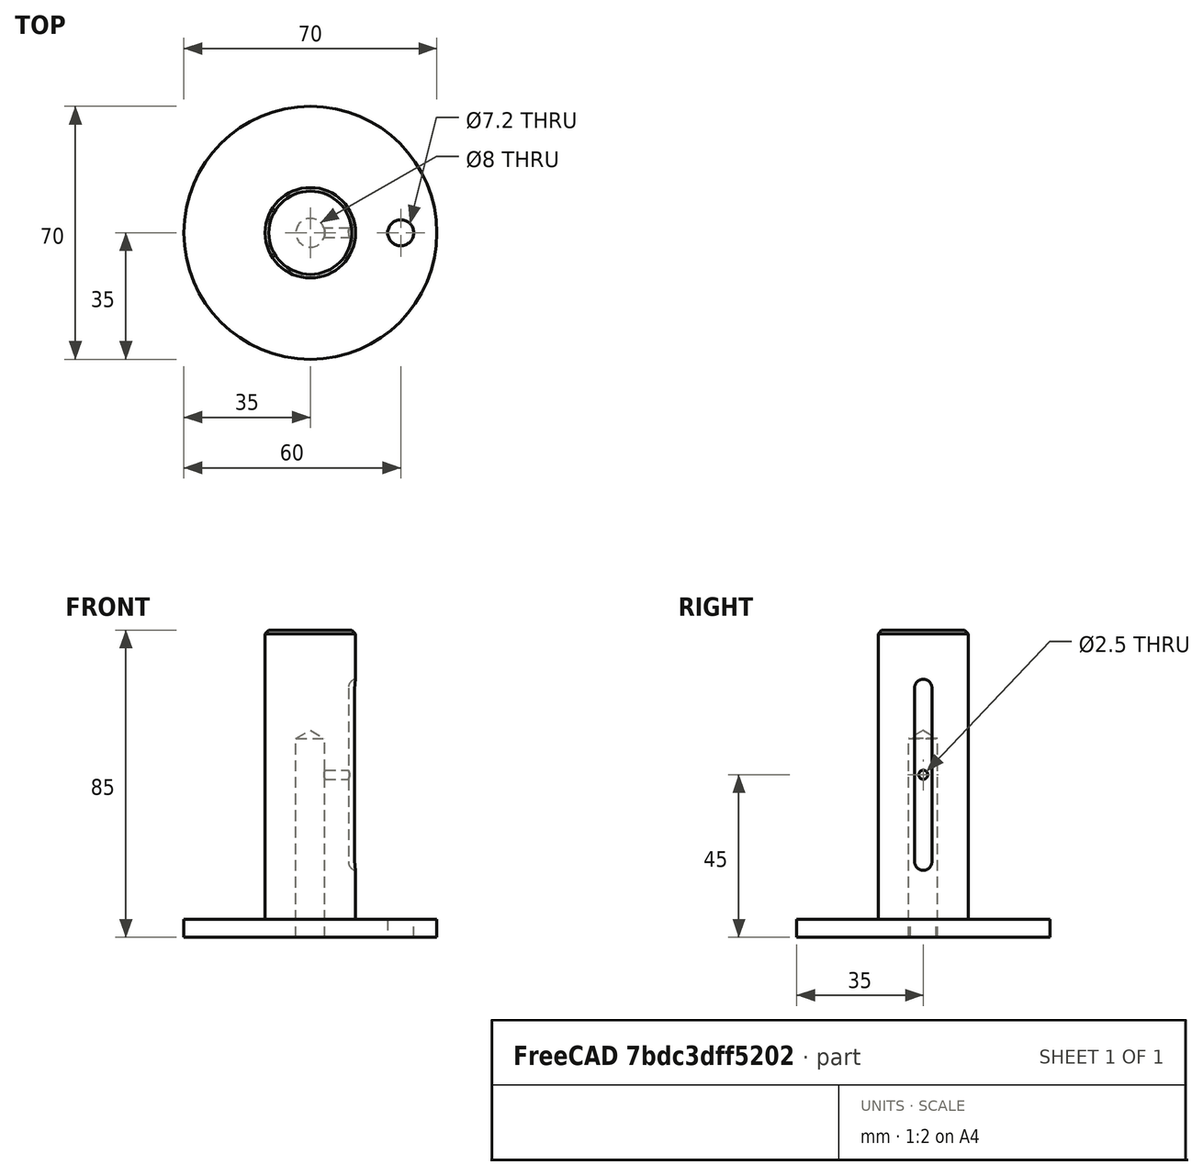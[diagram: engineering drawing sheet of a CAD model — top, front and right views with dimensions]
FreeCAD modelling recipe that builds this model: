
FCSTD DOCUMENT  (FreeCAD 0.20R29177 +426 (Git))
Label: hovair
License: All rights reserved
LicenseURL: http://en.wikipedia.org/wiki/All_rights_reserved
objects: Sketcher::SketchObject×8, TechDraw::DrawLeaderLine×5, TechDraw::DrawViewAnnotation×5, PartDesign::Plane×4, PartDesign::Pocket×4, TechDraw::DrawViewDimension×4, TechDraw::DrawViewSection×3, TechDraw::DrawViewBalloon×3, PartDesign::Revolution×2, PartDesign::Groove×2, PartDesign::Chamfer×2, TechDraw::DrawProjGroupItem×2, PartDesign::Body×1, TechDraw::DrawSVGTemplate×1, TechDraw::DrawProjGroup×1, TechDraw::DrawPage×1
note: 33 computed .brp shape members not serialized (recipe doc carries the construction recipe); baked Part::Feature solids carry a one-line shape summary decoded from their .brp

FEATURE [Sketcher::SketchObject] Sketch  label="axe sketch"
  FullyConstrained = true
  MapMode = 5
  Placement = pos=(0,0,0) rot=(1,0,0;1.5708rad)
  Support = -> [XZ_Plane]
  sketch-geometry (8):
    g0: LineSegment StartX=0 StartY=85 StartZ=0 EndX=-12.5 EndY=85 EndZ=0
    g1: LineSegment StartX=-12.5 StartY=85 StartZ=0 EndX=-12.5 EndY=5 EndZ=0
    g2: LineSegment StartX=-12.5 StartY=5 StartZ=0 EndX=-35 EndY=5 EndZ=0
    g3: LineSegment StartX=-35 StartY=5 StartZ=0 EndX=-35 EndY=0 EndZ=0
    g4: LineSegment StartX=-35 StartY=0 StartZ=0 EndX=-4 EndY=0 EndZ=0
    g5: LineSegment StartX=-4 StartY=0 StartZ=0 EndX=-4 EndY=55 EndZ=0
    g6: LineSegment StartX=-4 StartY=55 StartZ=0 EndX=0 EndY=57.3094 EndZ=0
    g7: LineSegment StartX=0 StartY=57.3094 StartZ=0 EndX=0 EndY=85 EndZ=0
  constraints (24):
    c: Horizontal(g0)
    c: Vertical(g1)
    c: Horizontal(g2)
    c: Vertical(g3)
    c: Horizontal(g4)
    c: Vertical(g5)
    c: Coincident(g6,g5)
    c: PointOnObject(g6,g-2)
    c: Coincident(g7,g6)
    c: Coincident(g0,g7)
    c: PointOnObject(g0,g-2)
    c: Coincident(g1,g0)
    c: Coincident(g2,g1)
    c: Coincident(g2,g3)
    c: Coincident(g4,g3)
    c: Coincident(g5,g4)
    c: Angle(g6,g-2) = 1.0472
    c: DistanceX(g4) = -4
    c: DistanceX(g3) = -35
    c: Distance(g3) = 5
    c: PointOnObject(g4,g-1)
    c: DistanceY(g1,g1) = 80
    c: Distance(g0) = 12.5
    c: DistanceY(g5) = 55
FEATURE [PartDesign::Revolution] Revolution  label="axe révolution"
  Angle = 360
  Axis = (0,2e-16,1)
  Base = (0,0,0)
  Placement = pos=(0,0,0) rot=(1,0,0;1.5708rad)
  Profile = -> Sketch
  ReferenceAxis = -> Sketch [V_Axis]
FEATURE [PartDesign::Plane] DatumPlane
  Length = 87.4941
  MapMode = 2
  Placement = pos=(0,0,0) rot=(1,0,0;1.5708rad)
  ResizeMode = 0
  Support = -> [Sketch]
  Width = 127.544
FEATURE [Sketcher::SketchObject] Sketch001  label="rainure sketch"
  FullyConstrained = false
  MapMode = 5
  Placement = pos=(0,0,0) rot=(1,0,0;1.5708rad)
  Support = -> [DatumPlane]
  sketch-geometry (5):
    g0: LineSegment StartX=13 StartY=71.5 StartZ=0 EndX=13 EndY=18.5 EndZ=0
    g1: LineSegment StartX=10.5 StartY=69 StartZ=0 EndX=10.5 EndY=21 EndZ=0
    g2: ArcOfCircle CenterX=13 CenterY=69 CenterZ=0 NormalX=0 NormalY=0 NormalZ=1 AngleXU=0 Radius=2.5 StartAngle=1.5708 EndAngle=3.14159
    g3: ArcOfCircle CenterX=13 CenterY=21 CenterZ=0 NormalX=0 NormalY=0 NormalZ=1 AngleXU=0 Radius=2.5 StartAngle=3.14159 EndAngle=4.71239
    g4: LineSegment StartX=13 StartY=82.5445 StartZ=0 EndX=13 EndY=14.5184 EndZ=0
  constraints (16):
    c: Vertical(g0)
    c: Vertical(g1)
    c: DistanceY(g0) = 18.5
    c: DistanceY(g1) = 21
    c: Distance(g1) = 48
    c: Distance(g0) = 53
    c: PointOnObject(g2,g0)
    c: Coincident(g2,g1)
    c: Coincident(g2,g0)
    c: Diameter(g2) = 5
    c: PointOnObject(g3,g0)
    c: Coincident(g3,g0)
    c: Coincident(g3,g1)
    c: DistanceX(g3) = 13
    c: Vertical(g4)
    c: PointOnObject(g2,g4)
FEATURE [PartDesign::Groove] Groove  label="rainure révolution"
  Angle = 360
  Axis = (0,-1.51e-14,-68.0261)
  Base = (13,1.83e-14,82.5445)
  BaseFeature = -> Revolution
  Placement = pos=(0,0,0) rot=(1,0,0;1.5708rad)
  Profile = -> Sketch001
  ReferenceAxis = -> Sketch001 [Axis0]
FEATURE [PartDesign::Plane] DatumPlane001
  AttachmentOffset = pos=(13,0,0) rot=(0,1,0;1.5708rad)
  Length = 87.522
  MapMode = 2
  Placement = pos=(13,0,0) rot=(0.57735,0.57735,0.57735;2.0944rad)
  ResizeMode = 0
  Support = -> [Sketch001]
  Width = 127.547
FEATURE [Sketcher::SketchObject] Sketch002  label="canal sketch"
  FullyConstrained = true
  MapMode = 5
  Placement = pos=(13,0,0) rot=(0.57735,0.57735,0.57735;2.0944rad)
  Support = -> [DatumPlane001]
  sketch-geometry (1):
    g0: Circle CenterX=0 CenterY=45 CenterZ=0 NormalX=0 NormalY=0 NormalZ=1 AngleXU=0 Radius=1.25
  constraints (3):
    c: Diameter(g0) = 2.5
    c: DistanceY(g0) = 45
    c: PointOnObject(g0,g-2)
FEATURE [PartDesign::Pocket] Pocket  label="canal extrusion"
  BaseFeature = -> Groove
  Direction = (-1,-2e-16,0)
  Length = 13
  Length2 = 5
  Placement = pos=(0,0,0) rot=(1,0,0;1.5708rad)
  Profile = -> Sketch002
  ReferenceAxis = -> Sketch002 [N_Axis]
  Type = 0
FEATURE [Sketcher::SketchObject] Sketch003
  FullyConstrained = true
  MapMode = 5
  Placement = pos=(0,1.1e-15,5) rot=(0,0,1;3.14159rad)
  Support = -> [Pocket]
  sketch-geometry (1):
    g0: Circle CenterX=-25 CenterY=0 CenterZ=0 NormalX=0 NormalY=0 NormalZ=1 AngleXU=0 Radius=3.6
  constraints (3):
    c: PointOnObject(g0,g-1)
    c: DistanceX(g0) = -25
    c: Diameter(g0) = 7.2
FEATURE [PartDesign::Pocket] Pocket001  label="trouFixation extrusion"
  BaseFeature = -> Pocket
  Direction = (0,-2e-16,-1)
  Length = 5
  Length2 = 5
  Placement = pos=(0,0,0) rot=(1,0,0;1.5708rad)
  Profile = -> Sketch003
  ReferenceAxis = -> Sketch003 [N_Axis]
  Type = 1
FEATURE [PartDesign::Chamfer] Chamfer
  Angle = 45
  Base = -> Pocket001 [Edge1]
  BaseFeature = -> Pocket001
  ChamferType = 0
  FlipDirection = false
  Placement = pos=(0,0,0) rot=(1,0,0;1.5708rad)
  Size = 1
  Size2 = 1
  SupportTransform = false
  UseAllEdges = false
FEATURE [PartDesign::Body] Body
  Group = -> [Sketch,Revolution,DatumPlane,Sketch001,Groove,DatumPlane001,Sketch002,Pocket,Sketch003,Pocket001,Chamfer]
  Origin = -> Origin
  Tip = -> Chamfer
FEATURE [TechDraw::DrawSVGTemplate] Template
  EditableTexts = Designed_by_Name=Designed by Name; Drawing_number=Drawing number; FC-Date=Date; FC-SC=Scale; FC-SH=Sheet; FC-Title=Title; Subtitle=Subtitle; Weight=Weight
  Height = 210
  Orientation = 1
  Width = 297
FEATURE [TechDraw::DrawProjGroupItem] ProjItem  label="Front"
  CoarseView = true
  Direction = (0,0,1)
  Focus = 100
  HardHidden = false
  IsoCount = 0
  IsoHidden = false
  IsoVisible = false
  LockPosition = true
  Perspective = false
  Rotation = 0
  RotationVector = (1,0,0)
  ScaleType = 2
  SeamHidden = false
  SeamVisible = true
  SmoothHidden = false
  SmoothVisible = true
  Source = -> [Chamfer]
  Type = 0
  X = 0
  XDirection = (1e-16,-1,0)
  Y = 0
FEATURE [TechDraw::DrawProjGroup] ProjGroup
  Anchor = -> ProjItem
  AutoDistribute = true
  LockPosition = false
  ProjectionType = 0
  Rotation = 0
  ScaleType = 0
  Source = -> [Chamfer]
  Views = -> [ProjItem]
  X = 238.43
  Y = 139.763
  spacingX = 15
  spacingY = 15
FEATURE [TechDraw::DrawViewSection] SectionView  label="Section  - "
  BaseView = -> ProjItem
  CoarseView = true
  CutSurfaceDisplay = 2
  Direction = (1e-16,-1,0)
  FileGeomPattern = <userpath>/AppData/Local/Programs/FreeCAD 0.20/data/Mod/TechDraw/PAT/FCPAT.pat
  FileHatchPattern = <userpath>/AppData/Local/Programs/FreeCAD 0.20/data/Mod/TechDraw/Patterns/simple.svg
  Focus = 100
  FuseBeforeCut = false
  HardHidden = false
  HatchScale = 1
  IsoCount = 0
  IsoHidden = false
  IsoVisible = false
  LockPosition = false
  NameGeomPattern = Diamant
  Perspective = false
  Rotation = 0
  ScaleType = 2
  SeamHidden = false
  SeamVisible = true
  SectionDirection = 1
  SectionNormal = (1e-16,-1,0)
  SectionOrigin = (-0.025,0,42.51)
  SmoothHidden = false
  SmoothVisible = true
  Source = -> [Chamfer]
  X = 126.918
  XDirection = (0,0,-1)
  Y = 138.146
FEATURE [TechDraw::DrawViewSection] SectionView001  label="Section  - 001"
  BaseView = -> SectionView
  CoarseView = true
  CutSurfaceDisplay = 2
  Direction = (0,0,-1)
  FileGeomPattern = <userpath>/AppData/Local/Programs/FreeCAD 0.20/data/Mod/TechDraw/PAT/FCPAT.pat
  FileHatchPattern = <userpath>/AppData/Local/Programs/FreeCAD 0.20/data/Mod/TechDraw/Patterns/simple.svg
  Focus = 100
  FuseBeforeCut = false
  HardHidden = false
  HatchScale = 1
  IsoCount = 0
  IsoHidden = false
  IsoVisible = false
  LockPosition = false
  NameGeomPattern = Diamant
  Perspective = false
  Rotation = 0
  ScaleType = 2
  SeamHidden = false
  SeamVisible = true
  SectionDirection = 1
  SectionNormal = (0,0,-1)
  SectionOrigin = (0,17.5,45)
  SmoothHidden = false
  SmoothVisible = true
  Source = -> [Chamfer]
  X = 33.4447
  XDirection = (-1e-16,1,0)
  Y = 139.013
FEATURE [TechDraw::DrawLeaderLine] LeaderLine
  AutoHorizontal = true
  EndSymbol = 7
  LeaderParent = -> SectionView
  LockPosition = true
  Rotation = 0
  Scalable = false
  ScaleType = 0
  StartSymbol = 7
  WayPoints = (1) [(0,0,0)]
  X = 0
  Y = 0
FEATURE [Sketcher::SketchObject] Sketch004  label="axe sketch001"
  FullyConstrained = true
  MapMode = 5
  Placement = pos=(0,0,0) rot=(1,0,0;1.5708rad)
  Support = -> [XZ_Plane001]
  sketch-geometry (8):
    g0: LineSegment StartX=0 StartY=85 StartZ=0 EndX=-12.5 EndY=85 EndZ=0
    g1: LineSegment StartX=-12.5 StartY=85 StartZ=0 EndX=-12.5 EndY=5 EndZ=0
    g2: LineSegment StartX=-12.5 StartY=5 StartZ=0 EndX=-35 EndY=5 EndZ=0
    g3: LineSegment StartX=-35 StartY=5 StartZ=0 EndX=-35 EndY=0 EndZ=0
    g4: LineSegment StartX=-35 StartY=0 StartZ=0 EndX=-4 EndY=0 EndZ=0
    g5: LineSegment StartX=-4 StartY=0 StartZ=0 EndX=-4 EndY=55 EndZ=0
    g6: LineSegment StartX=-4 StartY=55 StartZ=0 EndX=0 EndY=57.3094 EndZ=0
    g7: LineSegment StartX=0 StartY=57.3094 StartZ=0 EndX=0 EndY=85 EndZ=0
  constraints (24):
    c: Horizontal(g0)
    c: Vertical(g1)
    c: Horizontal(g2)
    c: Vertical(g3)
    c: Horizontal(g4)
    c: Vertical(g5)
    c: Coincident(g6,g5)
    c: PointOnObject(g6,g-2)
    c: Coincident(g7,g6)
    c: Coincident(g0,g7)
    c: PointOnObject(g0,g-2)
    c: Coincident(g1,g0)
    c: Coincident(g2,g1)
    c: Coincident(g2,g3)
    c: Coincident(g4,g3)
    c: Coincident(g5,g4)
    c: Angle(g6,g-2) = 1.0472
    c: DistanceX(g4) = -4
    c: DistanceX(g3) = -35
    c: Distance(g3) = 5
    c: PointOnObject(g4,g-1)
    c: DistanceY(g1,g1) = 80
    c: Distance(g0) = 12.5
    c: DistanceY(g5) = 55
FEATURE [PartDesign::Plane] DatumPlane002
  Length = 60
  MapMode = 2
  Placement = pos=(0,0,0) rot=(1,0,0;1.5708rad)
  ResizeMode = 0
  Support = -> [Sketch004]
  Width = 60
FEATURE [PartDesign::Revolution] Revolution001  label="axe révolution001"
  Angle = 360
  Axis = (0,2e-16,1)
  Base = (0,0,0)
  Placement = pos=(0,0,0) rot=(1,0,0;1.5708rad)
  Profile = -> Sketch004
  ReferenceAxis = -> Sketch004 [V_Axis]
FEATURE [Sketcher::SketchObject] Sketch005  label="rainure sketch001"
  FullyConstrained = false
  MapMode = 5
  Placement = pos=(0,0,0) rot=(1,0,0;1.5708rad)
  Support = -> [DatumPlane002]
  sketch-geometry (5):
    g0: LineSegment StartX=13 StartY=71.5 StartZ=0 EndX=13 EndY=18.5 EndZ=0
    g1: LineSegment StartX=10.5 StartY=69 StartZ=0 EndX=10.5 EndY=21 EndZ=0
    g2: ArcOfCircle CenterX=13 CenterY=69 CenterZ=0 NormalX=0 NormalY=0 NormalZ=1 AngleXU=0 Radius=2.5 StartAngle=1.5708 EndAngle=3.14159
    g3: ArcOfCircle CenterX=13 CenterY=21 CenterZ=0 NormalX=0 NormalY=0 NormalZ=1 AngleXU=0 Radius=2.5 StartAngle=3.14159 EndAngle=4.71239
    g4: LineSegment StartX=13 StartY=82.5445 StartZ=0 EndX=13 EndY=14.5184 EndZ=0
  constraints (16):
    c: Vertical(g0)
    c: Vertical(g1)
    c: DistanceY(g0) = 18.5
    c: DistanceY(g1) = 21
    c: Distance(g1) = 48
    c: Distance(g0) = 53
    c: PointOnObject(g2,g0)
    c: Coincident(g2,g1)
    c: Coincident(g2,g0)
    c: Diameter(g2) = 5
    c: PointOnObject(g3,g0)
    c: Coincident(g3,g0)
    c: Coincident(g3,g1)
    c: DistanceX(g3) = 13
    c: Vertical(g4)
    c: PointOnObject(g2,g4)
FEATURE [PartDesign::Plane] DatumPlane003
  AttachmentOffset = pos=(13,0,0) rot=(0,1,0;1.5708rad)
  Length = 60
  MapMode = 2
  Placement = pos=(13,0,0) rot=(0.57735,0.57735,0.57735;2.0944rad)
  ResizeMode = 0
  Support = -> [Sketch005]
  Width = 60
FEATURE [PartDesign::Groove] Groove001  label="rainure révolution001"
  Angle = 360
  Axis = (0,-1.51e-14,-68.0261)
  Base = (13,1.83e-14,82.5445)
  BaseFeature = -> Revolution001
  Placement = pos=(0,0,0) rot=(1,0,0;1.5708rad)
  Profile = -> Sketch005
  ReferenceAxis = -> Sketch005 [Axis0]
FEATURE [Sketcher::SketchObject] Sketch006  label="canal sketch001"
  FullyConstrained = true
  MapMode = 5
  Placement = pos=(13,0,0) rot=(0.57735,0.57735,0.57735;2.0944rad)
  Support = -> [DatumPlane003]
  sketch-geometry (1):
    g0: Circle CenterX=0 CenterY=45 CenterZ=0 NormalX=0 NormalY=0 NormalZ=1 AngleXU=0 Radius=1.25
  constraints (3):
    c: Diameter(g0) = 2.5
    c: DistanceY(g0) = 45
    c: PointOnObject(g0,g-2)
FEATURE [PartDesign::Pocket] Pocket002  label="canal extrusion001"
  BaseFeature = -> Groove001
  Direction = (-1,-2e-16,0)
  Length = 13
  Length2 = 5
  Placement = pos=(0,0,0) rot=(1,0,0;1.5708rad)
  Profile = -> Sketch006
  ReferenceAxis = -> Sketch006 [N_Axis]
  Type = 0
FEATURE [Sketcher::SketchObject] Sketch007
  FullyConstrained = true
  MapMode = 5
  Placement = pos=(0,3.3e-15,5) rot=(0,0,1;3.14159rad)
  Support = -> [Pocket002]
  sketch-geometry (1):
    g0: Circle CenterX=-25 CenterY=0 CenterZ=0 NormalX=0 NormalY=0 NormalZ=1 AngleXU=0 Radius=3.6
  constraints (3):
    c: PointOnObject(g0,g-1)
    c: DistanceX(g0) = -25
    c: Diameter(g0) = 7.2
FEATURE [PartDesign::Pocket] Pocket003  label="trouFixation extrusion001"
  BaseFeature = -> Pocket002
  Direction = (0,-2e-16,-1)
  Length = 5
  Length2 = 5
  Placement = pos=(0,0,0) rot=(1,0,0;1.5708rad)
  Profile = -> Sketch007
  ReferenceAxis = -> Sketch007 [N_Axis]
  Type = 1
FEATURE [PartDesign::Chamfer] Chamfer001
  Angle = 45
  Base = -> Pocket003 [Edge1]
  BaseFeature = -> Pocket003
  ChamferType = 0
  FlipDirection = false
  Placement = pos=(0,0,0) rot=(1,0,0;1.5708rad)
  Size = 1
  Size2 = 1
  SupportTransform = false
  UseAllEdges = false
FEATURE [TechDraw::DrawProjGroupItem] ProjItem002  label="Front001"
  CoarseView = true
  Direction = (0,0,1)
  Focus = 100
  HardHidden = false
  IsoCount = 0
  IsoHidden = false
  IsoVisible = false
  LockPosition = true
  Perspective = false
  Rotation = 0
  RotationVector = (1,0,0)
  ScaleType = 2
  SeamHidden = false
  SeamVisible = true
  SmoothHidden = false
  SmoothVisible = true
  Source = -> [Chamfer001]
  Type = 0
  X = 0
  XDirection = (1e-16,-1,0)
  Y = 0
FEATURE [TechDraw::DrawViewSection] SectionView002  label="Section  - 002"
  BaseView = -> ProjItem002
  CoarseView = false
  CutSurfaceDisplay = 2
  Direction = (1e-16,-1,0)
  FileGeomPattern = <userpath>/AppData/Local/Programs/FreeCAD 0.20/data/Mod/TechDraw/PAT/FCPAT.pat
  FileHatchPattern = <userpath>/AppData/Local/Programs/FreeCAD 0.20/data/Mod/TechDraw/Patterns/simple.svg
  Focus = 100
  FuseBeforeCut = false
  HardHidden = false
  HatchScale = 1
  IsoCount = 0
  IsoHidden = false
  IsoVisible = false
  LockPosition = false
  NameGeomPattern = Diamant
  Perspective = false
  Rotation = 0
  ScaleType = 2
  SeamHidden = false
  SeamVisible = true
  SectionDirection = 1
  SectionNormal = (1e-16,-1,0)
  SectionOrigin = (-0.025,0,42.51)
  SmoothHidden = false
  SmoothVisible = true
  Source = -> [Chamfer001]
  X = 137.588
  XDirection = (0,0,-1)
  Y = 139.782
FEATURE [TechDraw::DrawViewDimension] Dimension
  AngleOverride = false
  Arbitrary = false
  ArbitraryTolerances = false
  EqualTolerance = true
  ExtensionAngle = 0
  FormatSpec = %.2w
  FormatSpecOverTolerance = %+.2w
  FormatSpecUnderTolerance = %+.2w
  Inverted = false
  LineAngle = 0
  LockPosition = false
  MeasureType = 1
  OverTolerance = 0
  References2D = -> [ProjItem]
  Rotation = 0
  ScaleType = 0
  TheoreticalExact = false
  Type = 2
  UnderTolerance = 0
  X = 41.9494
  Y = 14.7997
FEATURE [TechDraw::DrawViewDimension] Dimension001
  AngleOverride = false
  Arbitrary = false
  ArbitraryTolerances = false
  EqualTolerance = true
  ExtensionAngle = 0
  FormatSpec = ⌀%.2w
  FormatSpecOverTolerance = %+.2w
  FormatSpecUnderTolerance = %+.2w
  Inverted = false
  LineAngle = 0
  LockPosition = false
  MeasureType = 1
  OverTolerance = 0
  References2D = -> [ProjItem]
  Rotation = 0
  ScaleType = 0
  TheoreticalExact = false
  Type = 5
  UnderTolerance = 0
  X = -11.1546
  Y = 51.8817
FEATURE [TechDraw::DrawViewAnnotation] Annotation
  Font = osifont
  LineSpace = 80
  LockPosition = false
  MaxWidth = -1
  Rotation = 0
  ScaleType = 0
  Text = A
  TextSize = 5
  TextStyle = 0
  X = 249.41
  Y = 96.4395
FEATURE [TechDraw::DrawViewAnnotation] Annotation001
  Font = osifont
  LineSpace = 80
  LockPosition = false
  MaxWidth = -1
  Rotation = 0
  ScaleType = 0
  Text = A
  TextSize = 5
  TextStyle = 0
  X = 248.632
  Y = 186.973
FEATURE [TechDraw::DrawViewAnnotation] Annotation002
  Font = osifont
  LineSpace = 80
  LockPosition = false
  MaxWidth = -1
  Rotation = 0
  ScaleType = 0
  Text = A - A
  TextSize = 5
  TextStyle = 0
  X = 73.8133
  Y = 190.467
FEATURE [TechDraw::DrawViewAnnotation] Annotation003
  Font = osifont
  LineSpace = 80
  LockPosition = false
  MaxWidth = -1
  Rotation = 0
  ScaleType = 0
  Text = M10
  TextSize = 5
  TextStyle = 0
  X = 175.133
  Y = 124.543
FEATURE [TechDraw::DrawLeaderLine] LeaderLine002
  AutoHorizontal = true
  EndSymbol = 7
  LeaderParent = -> SectionView
  LockPosition = true
  Rotation = 0
  Scalable = false
  ScaleType = 0
  StartSymbol = 7
  WayPoints = (1) [(0,0,0)]
  X = 13.9634
  Y = 4.98905
FEATURE [TechDraw::DrawLeaderLine] LeaderLine003
  AutoHorizontal = true
  EndSymbol = 7
  LeaderParent = -> SectionView
  LockPosition = true
  Rotation = 0
  Scalable = false
  ScaleType = 0
  StartSymbol = 7
  WayPoints = (1) [(0,0,0)]
  X = 13.9843
  Y = 4.94774
FEATURE [TechDraw::DrawViewBalloon] Balloon
  BubbleShape = 5
  EndType = 0
  EndTypeScale = 1
  KinkLength = 5
  LockPosition = false
  OriginX = -35.2247
  OriginY = 12.5
  Rotation = 0
  ScaleType = 0
  ShapeScale = 1
  SourceView = -> SectionView
  Text = 3.2
  TextWrapLen = -1
  X = -18.3506
  Y = 23.975
FEATURE [TechDraw::DrawViewBalloon] Balloon001
  BubbleShape = 5
  EndType = 0
  EndTypeScale = 1
  KinkLength = 5
  LockPosition = false
  OriginX = 37.5
  OriginY = -35
  Rotation = 0
  ScaleType = 0
  ShapeScale = 1
  SourceView = -> SectionView
  Text = ⟂| 0,05
  TextWrapLen = -1
  X = -46.2212
  Y = -34.8917
FEATURE [TechDraw::DrawLeaderLine] LeaderLine004
  AutoHorizontal = true
  EndSymbol = 7
  LeaderParent = -> SectionView
  LockPosition = true
  Rotation = 0
  Scalable = false
  ScaleType = 0
  StartSymbol = 7
  WayPoints = (3) [(0,0,0),(0,-256.456,0),(248.116,-256.456,0)]
  X = -47.9828
  Y = -25.695
FEATURE [TechDraw::DrawLeaderLine] LeaderLine005
  AutoHorizontal = true
  EndSymbol = 7
  LeaderParent = -> SectionView
  LockPosition = true
  Rotation = 0
  Scalable = false
  ScaleType = 0
  StartSymbol = 7
  WayPoints = (4) [(0,0,0),(-301.284,-1.0425,0),(-301.284,117.803,0),(0,117.803,0)]
  X = 42.5224
  Y = 5.7009
FEATURE [TechDraw::DrawViewBalloon] Balloon002
  BubbleShape = 7
  EndType = 0
  EndTypeScale = 1
  KinkLength = 5
  LockPosition = false
  OriginX = 1.44097
  OriginY = 10.9705
  Rotation = 0
  ScaleType = 0
  ShapeScale = 1
  SourceView = -> SectionView001
  Text = R2.5
  TextWrapLen = -1
  X = -15.6259
  Y = 30.319
FEATURE [TechDraw::DrawViewAnnotation] Annotation004
  Font = osifont
  LineSpace = 80
  LockPosition = false
  MaxWidth = -1
  Rotation = 0
  ScaleType = 0
  Text = B - B
  TextSize = 5
  TextStyle = 0
  X = 23.6726
  Y = 190.294
FEATURE [TechDraw::DrawViewDimension] Dimension002
  AngleOverride = false
  Arbitrary = false
  ArbitraryTolerances = false
  EqualTolerance = true
  ExtensionAngle = 0
  FormatSpec = %.2w
  FormatSpecOverTolerance = %+.2w
  FormatSpecUnderTolerance = %+.2w
  Inverted = false
  LineAngle = 0
  LockPosition = false
  MeasureType = 1
  OverTolerance = 0
  References2D = -> [SectionView]
  Rotation = 0
  ScaleType = 0
  TheoreticalExact = false
  Type = 2
  UnderTolerance = 0
  X = 51.3275
  Y = -10.1297
FEATURE [TechDraw::DrawViewDimension] Dimension003
  AngleOverride = false
  Arbitrary = false
  ArbitraryTolerances = false
  EqualTolerance = true
  ExtensionAngle = 0
  FormatSpec = %.2w
  FormatSpecOverTolerance = %+.2w
  FormatSpecUnderTolerance = %+.2w
  Inverted = false
  LineAngle = 0
  LockPosition = false
  MeasureType = 1
  OverTolerance = 0
  References2D = -> [SectionView]
  Rotation = 0
  ScaleType = 0
  TheoreticalExact = false
  Type = 2
  UnderTolerance = 0
  X = 59.5497
  Y = 3.14852
FEATURE [TechDraw::DrawPage] Page
  KeepUpdated = true
  NextBalloonIndex = 4
  ProjectionType = 0
  Template = -> Template
  Views = -> [ProjGroup,SectionView,SectionView001,LeaderLine,Dimension,Dimension001,Annotation,Annotation001,Annotation002,Annotation003,LeaderLine002,LeaderLine003,Balloon,Balloon001,LeaderLine004,LeaderLine005,Balloon002,Annotation004,Dimension002,Dimension003]
